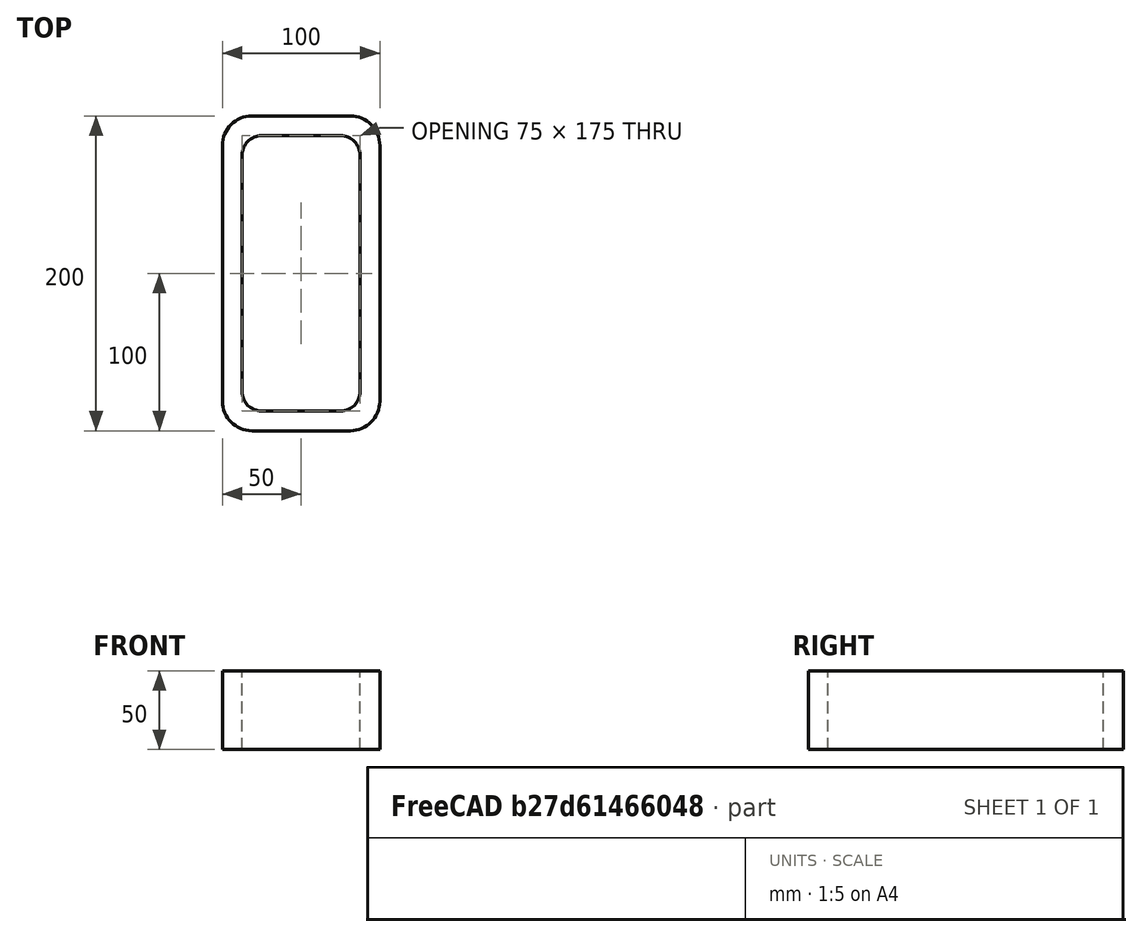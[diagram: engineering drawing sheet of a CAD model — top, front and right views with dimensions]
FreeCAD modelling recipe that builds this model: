
FCSTD DOCUMENT  (FreeCAD 0.15R4671 (Git))
Label: Rectangular hollow section 200x100x12.5 EN10219 S235JRH
License: All rights reserved
LicenseURL: http://en.wikipedia.org/wiki/All_rights_reserved
objects: Sketcher::SketchObject×1, Part::Extrusion×1
note: 2 computed .brp shape members not serialized (recipe doc carries the construction recipe); baked Part::Feature solids carry a one-line shape summary decoded from their .brp

FEATURE [Sketcher::SketchObject] Sketch
  sketch-geometry (16):
    g0: LineSegment StartX=-25 StartY=87.5 StartZ=0 EndX=25 EndY=87.5 EndZ=0
    g1: LineSegment StartX=37.5 StartY=75 StartZ=0 EndX=37.5 EndY=-75 EndZ=0
    g2: LineSegment StartX=25 StartY=-87.5 StartZ=0 EndX=-25 EndY=-87.5 EndZ=0
    g3: LineSegment StartX=-37.5 StartY=-75 StartZ=0 EndX=-37.5 EndY=75 EndZ=0
    g4: LineSegment StartX=-31.25 StartY=100 StartZ=0 EndX=31.25 EndY=100 EndZ=0
    g5: LineSegment StartX=50 StartY=81.25 StartZ=0 EndX=50 EndY=-81.25 EndZ=0
    g6: LineSegment StartX=31.25 StartY=-100 StartZ=0 EndX=-31.25 EndY=-100 EndZ=0
    g7: LineSegment StartX=-50 StartY=-81.25 StartZ=0 EndX=-50 EndY=81.25 EndZ=0
    g8: ArcOfCircle CenterX=-25 CenterY=75 CenterZ=0 NormalX=0 NormalY=0 NormalZ=1 Radius=12.5 StartAngle=1.5708 EndAngle=3.14159
    g9: ArcOfCircle CenterX=25 CenterY=75 CenterZ=0 NormalX=0 NormalY=0 NormalZ=1 Radius=12.5 StartAngle=0 EndAngle=1.5708
    g10: ArcOfCircle CenterX=25 CenterY=-75 CenterZ=0 NormalX=0 NormalY=0 NormalZ=1 Radius=12.5 StartAngle=4.71239 EndAngle=6.28319
    g11: ArcOfCircle CenterX=-25 CenterY=-75 CenterZ=0 NormalX=0 NormalY=0 NormalZ=1 Radius=12.5 StartAngle=3.14159 EndAngle=4.71239
    g12: ArcOfCircle CenterX=31.25 CenterY=81.25 CenterZ=0 NormalX=0 NormalY=0 NormalZ=1 Radius=18.75 StartAngle=0 EndAngle=1.5708
    g13: ArcOfCircle CenterX=31.25 CenterY=-81.25 CenterZ=0 NormalX=0 NormalY=0 NormalZ=1 Radius=18.75 StartAngle=4.71239 EndAngle=6.28319
    g14: ArcOfCircle CenterX=-31.25 CenterY=-81.25 CenterZ=0 NormalX=0 NormalY=0 NormalZ=1 Radius=18.75 StartAngle=3.14159 EndAngle=4.71239
    g15: ArcOfCircle CenterX=-31.25 CenterY=81.25 CenterZ=0 NormalX=0 NormalY=0 NormalZ=1 Radius=18.75 StartAngle=1.5708 EndAngle=3.14159
  constraints (36):
    c: Horizontal(g2)
    c: Vertical(g3)
    c: Horizontal(g6)
    c: Vertical(g7)
    c: Tangent(g3,g8) = 1.5708
    c: Tangent(g0,g8) = 1.5708
    c: Tangent(g0,g9) = 1.5708
    c: Tangent(g1,g9) = 1.5708
    c: Tangent(g1,g10) = 1.5708
    c: Tangent(g2,g10) = 1.5708
    c: Tangent(g2,g11) = 1.5708
    c: Tangent(g3,g11) = 1.5708
    c: Tangent(g4,g12) = 1.5708
    c: Tangent(g5,g12) = 1.5708
    c: Tangent(g5,g13) = 1.5708
    c: Tangent(g6,g13) = 1.5708
    c: Tangent(g6,g14) = 1.5708
    c: Tangent(g7,g14) = 1.5708
    c: Tangent(g7,g15) = 1.5708
    c: Tangent(g4,g15) = 1.5708
    c: Equal(g9,g8)
    c: Equal(g9,g11)
    c: Equal(g9,g10)
    c: Equal(g12,g15)
    c: Equal(g12,g14)
    c: Equal(g12,g13)
    c: Symmetric(g4,g6,g-1)
    c: Symmetric(g7,g5,g-2)
    c: DistanceY(g4,g6) = -200
    c: DistanceX(g7,g5) = 100
    c: Symmetric(g3,g1,g-2)
    c: Symmetric(g0,g2,g-1)
    c: DistanceY(g0,g4) = 12.5
    c: DistanceX(g5,g1) = -12.5
    c: Radius(g9) = 12.5
    c: Radius(g12) = 18.75
FEATURE [Part::Extrusion] Extrude  label="Rectangular hollow section 200x100x12.5 EN10219 S235JRH"
  Base = -> Sketch
  Dir = (0,0,50)
  Solid = true
